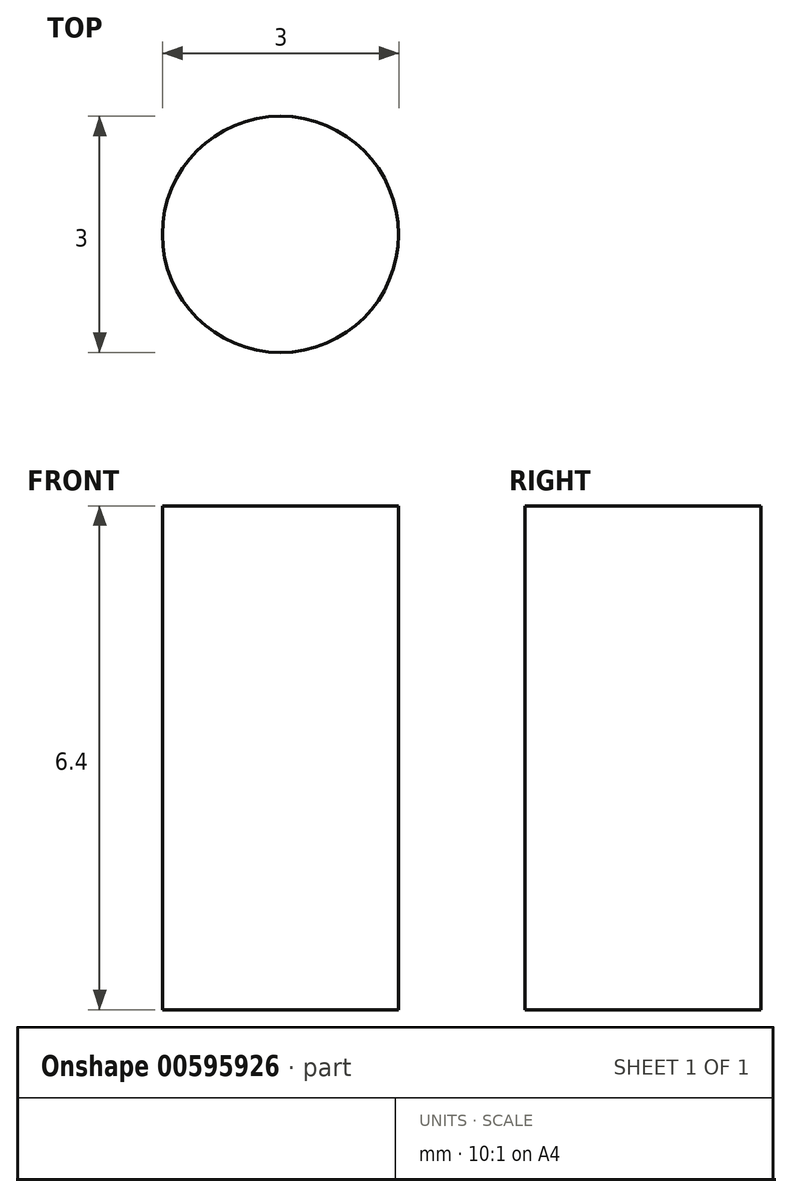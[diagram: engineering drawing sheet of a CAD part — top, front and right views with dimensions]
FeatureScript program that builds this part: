
annotation { "Feature Type Name" : "Feature", "Feature Type Description" : "" }
export const myFeature = defineFeature(function(context is Context, id is Id, definition is map)
    precondition{}
    {
        {
            var Q0;
            Q0=qCreatedBy(makeId("Top.planeOp"),FACE);
            var sketch = newSketch(context, id + "F0", { "sketchPlane" : qUnion([Q0])});
            skCircle(sketch, "E0", {"center": v(-19.8, 17.73) * mm, "radius": 1.5 * mm});
            skPoint(sketch, "E0.first.point", {"position": v(-21.3, 17.72) * mm});
            skPoint(sketch, "E0.second.point", {"position": v(-19.55, 16.25) * mm});
            skPoint(sketch, "E0.third.point", {"position": v(-20.33, 16.33) * mm});
            skSolve(sketch);
        }
        {
            var Q0;
            Q0=qSketchRegion(id+"F0",true);
            extrude(context, id + "F1", {"entities" : qUnion([Q0]), "depth" : 6.4 * mm, "offsetDistance" : 25 * mm});
        }
    });
